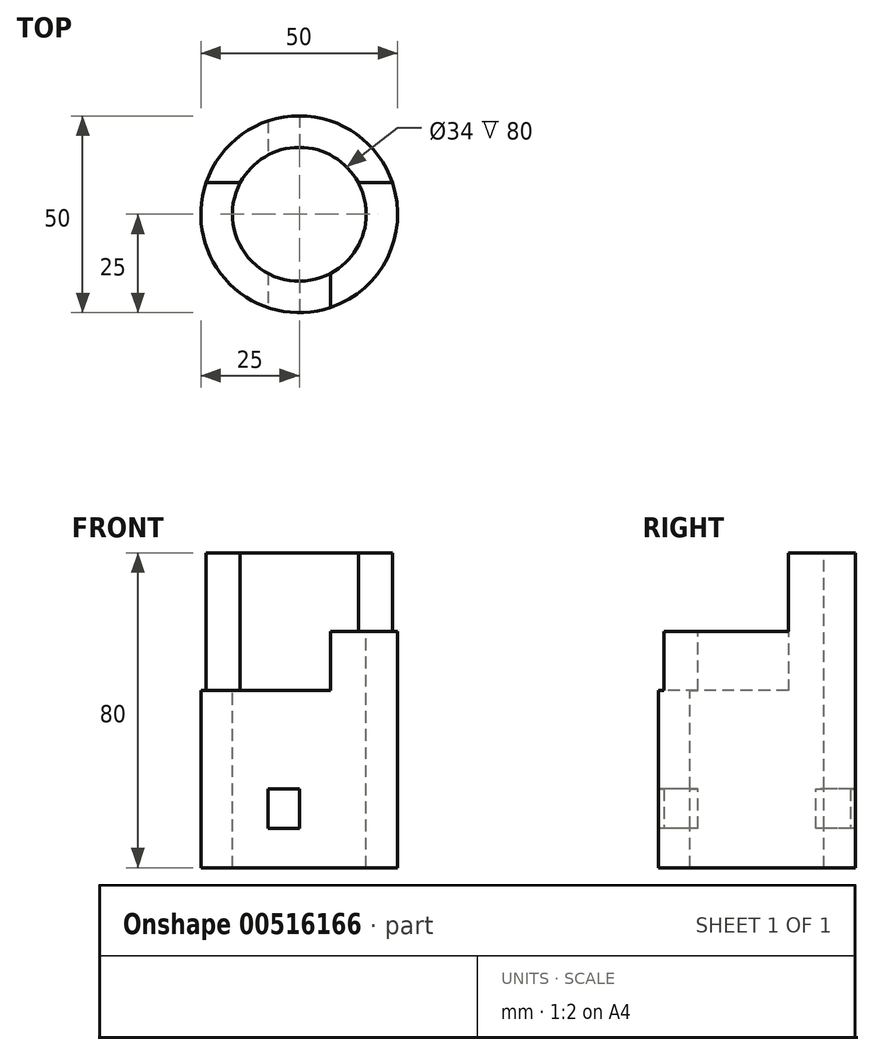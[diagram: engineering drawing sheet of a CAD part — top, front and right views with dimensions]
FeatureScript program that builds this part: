
annotation { "Feature Type Name" : "Feature", "Feature Type Description" : "" }
export const myFeature = defineFeature(function(context is Context, id is Id, definition is map)
    precondition{}
    {
        {
            var Q0;
            Q0=qCreatedBy(makeId("Top.planeOp"),FACE);
            var sketch = newSketch(context, id + "F0", { "sketchPlane" : qUnion([Q0])});
            skCircle(sketch, "E0", {"center": v(0, 0) * mm, "radius": 25 * mm});
            skSolve(sketch);
        }
        {
            var Q0;
            Q0=makeQuery(id+"F0.imprint","IMPRINT",FACE,{"disambiguationData":[TD([[makeQuery(id+"F0.imprint","IMPRINT",EDGE,{"derivedFrom":sQuery(id+"F0.wireOp",EDGE,"E0")}),1.0]])]});
            extrude(context, id + "F1", {"entities" : qUnion([Q0]), "depth" : 80 * mm, "offsetDistance" : 25 * mm});
        }
        {
            var Q0;
            Q0=makeQuery(id+"F1.opExtrude","CAP_FACE",FACE,{"disambiguationData":[OSD([sQuery(id+"F0.wireOp",EDGE,"E0")])],"isStart":false});
            var sketch = newSketch(context, id + "F2", { "sketchPlane" : qUnion([Q0])});
            skCircle(sketch, "E1", {"center": v(0, 0) * mm, "radius": 17 * mm});
            skSolve(sketch);
        }
        {
            var Q0;
            Q0=makeQuery(id+"F2.imprint","IMPRINT",FACE,{"disambiguationData":[TD([[makeQuery(id+"F2.imprint","IMPRINT",EDGE,{"derivedFrom":sQuery(id+"F2.wireOp",EDGE,"E1")}),1.0]])]});
            extrude(context, id + "F3", {"entities" : qUnion([Q0]), "operationType" : NewBodyOperationType.REMOVE, "oppositeDirection" : true, "depth" : 80 * mm, "offsetDistance" : 25 * mm});
        }
        {
            var Q0;
            Q0=qCreatedBy(makeId("Front.planeOp"),FACE);
            cPlane(context, id + "F4", {"entities" : qUnion([Q0]), "cplaneType" : CPlaneType.OFFSET, "offset" : 25 * mm, "width" : 150 * mm, "height" : 150 * mm});
        }
        {
            var Q0;
            Q0=qCreatedBy(id+"F4.planeOp",FACE);
            var sketch = newSketch(context, id + "F5", { "sketchPlane" : qUnion([Q0])});
            skLineSegment(sketch, "E2", {"start": v(0, 0) * mm, "end": v(0, 80) * mm});
            skLineSegment(sketch, "E3", {"start": v(0, 0) * mm, "end": v(25, 0) * mm});
            skLineSegment(sketch, "E4", {"start": v(25, 0) * mm, "end": v(25, 80) * mm});
            skLineSegment(sketch, "E5", {"start": v(25, 80) * mm, "end": v(25, 60) * mm});
            skLineSegment(sketch, "E6", {"start": v(25, 80) * mm, "end": v(25, 45) * mm});
            skLineSegment(sketch, "E7", {"start": v(25, 45) * mm, "end": v(-25, 45) * mm});
            skLineSegment(sketch, "E8", {"start": v(0, 80) * mm, "end": v(8, 80) * mm});
            skLineSegment(sketch, "E9", {"start": v(25, 60) * mm, "end": v(8, 60) * mm});
            skLineSegment(sketch, "E10", {"start": v(8, 60) * mm, "end": v(8, 45) * mm});
            skLineSegment(sketch, "E11", {"start": v(-25, 45) * mm, "end": v(-25, 80) * mm});
            skLineSegment(sketch, "E12", {"start": v(-25, 80) * mm, "end": v(25, 80) * mm});
            skLineSegment(sketch, "E13", {"start": v(25, 0) * mm, "end": v(25, 10) * mm});
            skLineSegment(sketch, "E14", {"start": v(25, 10) * mm, "end": v(-8, 10) * mm});
            skLineSegment(sketch, "E15", {"start": v(-8, 10) * mm, "end": v(-8, 20) * mm});
            skLineSegment(sketch, "E16", {"start": v(-8, 20) * mm, "end": v(25, 20) * mm});
            skLineSegment(sketch, "E17", {"start": v(25, 20) * mm, "end": v(25, 10) * mm});
            skSolve(sketch);
        }
        {
            var Q0;
            {var subQ4=sQuery(id+"F5.wireOp",EDGE,"E9");Q0=makeQuery(id+"F5.imprint","IMPRINT",FACE,{"disambiguationData":[TD([[makeQuery(id+"F5.imprint","IMPRINT",EDGE,{"derivedFrom":subQ4}),-1.0]])]});}
            var Q1;
            {var subQ5=sQuery(id+"F5.wireOp",EDGE,"E11");Q1=makeQuery(id+"F5.imprint","IMPRINT",FACE,{"disambiguationData":[TD([[makeQuery(id+"F5.imprint","IMPRINT",EDGE,{"derivedFrom":subQ5}),-1.0]])]});}
            extrude(context, id + "F6", {"entities" : qUnion([Q0, Q1]), "operationType" : NewBodyOperationType.REMOVE, "oppositeDirection" : true, "depth" : 33 * mm, "offsetDistance" : 25 * mm});
        }
        {
            var Q0;
            {var subQ5=sQuery(id+"F5.wireOp",EDGE,"E15");Q0=makeQuery(id+"F5.imprint","IMPRINT",FACE,{"disambiguationData":[TD([[makeQuery(id+"F5.imprint","IMPRINT",EDGE,{"derivedFrom":subQ5}),-1.0]])]});}
            var Q1;
            {var subQ5=sQuery(id+"F5.wireOp",EDGE,"E17");Q1=makeQuery(id+"F5.imprint","IMPRINT",FACE,{"disambiguationData":[TD([[makeQuery(id+"F5.imprint","IMPRINT",EDGE,{"derivedFrom":subQ5}),-1.0]])]});}
            extrude(context, id + "F7", {"entities" : qUnion([Q0, Q1]), "operationType" : NewBodyOperationType.REMOVE, "oppositeDirection" : true, "depth" : 50 * mm, "offsetDistance" : 25 * mm});
        }
    });
